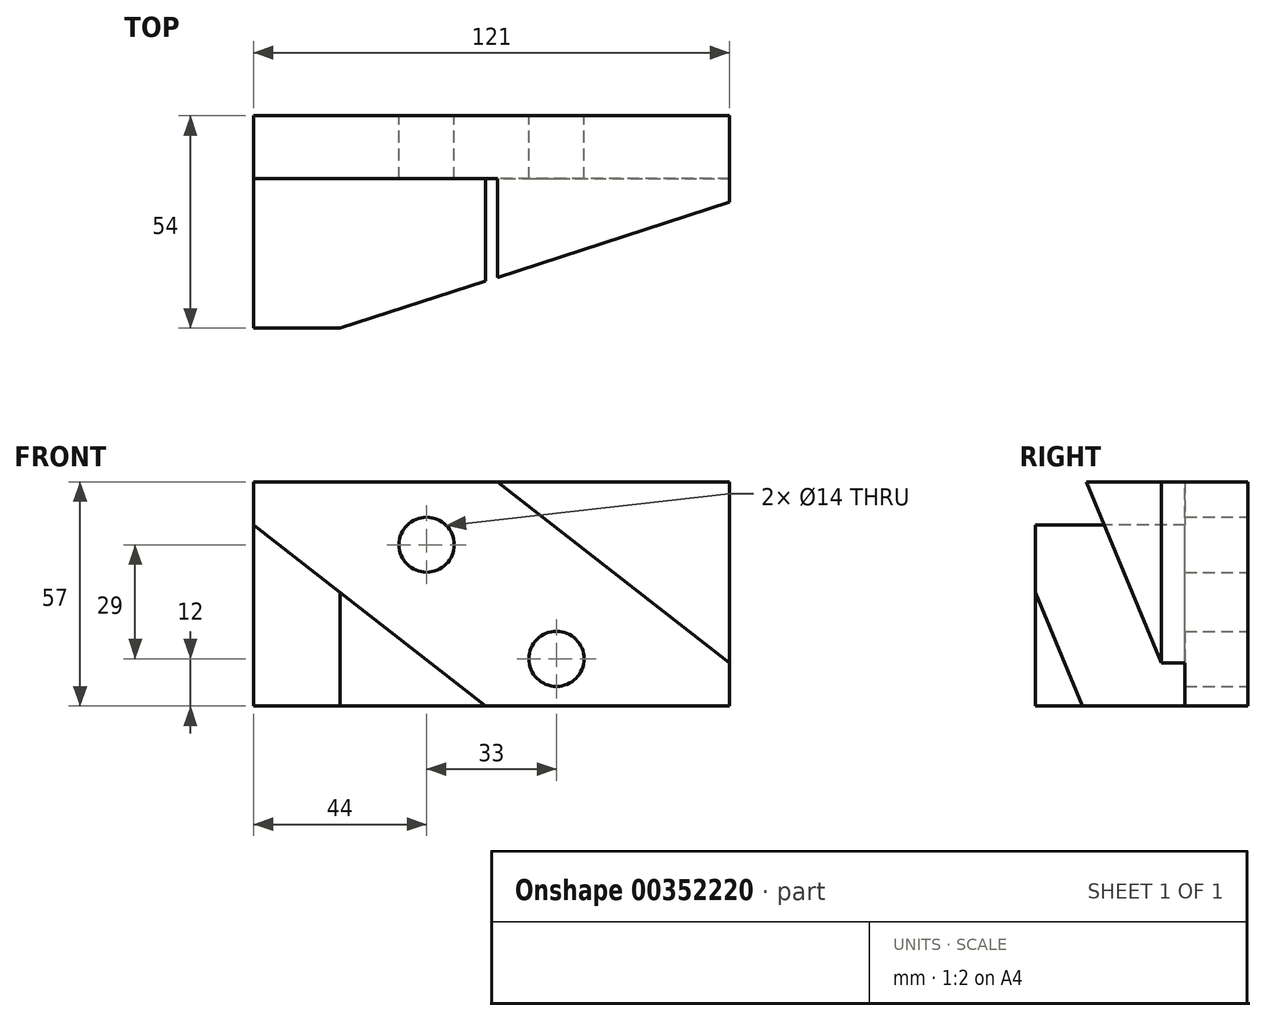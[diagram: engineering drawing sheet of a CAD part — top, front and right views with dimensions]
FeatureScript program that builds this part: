
annotation { "Feature Type Name" : "Feature", "Feature Type Description" : "" }
export const myFeature = defineFeature(function(context is Context, id is Id, definition is map)
    precondition{}
    {
        {
            var Q0;
            Q0=qCreatedBy(makeId("Front.planeOp"),FACE);
            var sketch = newSketch(context, id + "F0", { "sketchPlane" : qUnion([Q0])});
            skLineSegment(sketch, "E0", {"start": v(0, 0) * mm, "end": v(121, 0) * mm});
            skLineSegment(sketch, "E1", {"start": v(121, 0) * mm, "end": v(121, 57) * mm});
            skLineSegment(sketch, "E2", {"start": v(121, 57) * mm, "end": v(0, 57) * mm});
            skLineSegment(sketch, "E3", {"start": v(0, 57) * mm, "end": v(0, 0) * mm});
            skSolve(sketch);
        }
        {
            var Q0;
            Q0 = qSketchRegion(id + "F0", true);
            extrude(context, id + "F1", {"entities" : qUnion([Q0]), "depth" : 54 * mm});
        }
        {
            var Q0;
            Q0=makeQuery(id+"F1.opExtrude","SWEPT_FACE",FACE,{"disambiguationData":[OSD([sQuery(id+"F0.wireOp",EDGE,"E2")])]});
            var sketch = newSketch(context, id + "F2", { "sketchPlane" : qUnion([Q0])});
            skLineSegment(sketch, "E4", {"start": v(0, -54) * mm, "end": v(22, -54) * mm});
            skLineSegment(sketch, "E5", {"start": v(121, 0) * mm, "end": v(121, -16) * mm});
            skLineSegment(sketch, "E6", {"start": v(121, -16) * mm, "end": v(121, -22) * mm});
            skLineSegment(sketch, "E7", {"start": v(121, -22) * mm, "end": v(22, -54) * mm});
            skLineSegment(sketch, "E8", {"start": v(121, -22) * mm, "end": v(121, -54) * mm});
            skLineSegment(sketch, "E9", {"start": v(121, -54) * mm, "end": v(22, -54) * mm});
            skSolve(sketch);
        }
        {
            var Q0;
            Q0=makeQuery(id+"F2.imprint","IMPRINT",FACE,{"disambiguationData":[TD([[makeQuery(id+"F2.imprint","IMPRINT",EDGE,{"derivedFrom":sQuery(id+"F2.wireOp",EDGE,"E7")}),1.0]])]});
            extrude(context, id + "F3", {"entities" : qUnion([Q0]), "operationType" : NewBodyOperationType.REMOVE, "endBound" : BoundingType.THROUGH_ALL, "oppositeDirection" : true, "depth" : 25 * mm});
        }
        {
            var Q0;
            Q0=qCreatedBy(makeId("Front.planeOp"),FACE);
            var sketch = newSketch(context, id + "F4", { "sketchPlane" : qUnion([Q0])});
            skCircle(sketch, "E10", {"center": v(44, 41) * mm, "radius": 7 * mm});
            skCircle(sketch, "E11", {"center": v(77, 12) * mm, "radius": 7 * mm});
            skLineSegment(sketch, "E12.0.0", {"start": v(0, 0) * mm, "end": v(22, 0) * mm});
            skLineSegment(sketch, "E12.0.1", {"start": v(22, 0) * mm, "end": v(22, 57) * mm});
            skLineSegment(sketch, "E12.0.2", {"start": v(22, 57) * mm, "end": v(0, 57) * mm});
            skLineSegment(sketch, "E12.0.3", {"start": v(0, 57) * mm, "end": v(0, 0) * mm});
            skLineSegment(sketch, "E13.0", {"start": v(121, 57) * mm, "end": v(22, 57) * mm});
            skLineSegment(sketch, "E14.0.0", {"start": v(121, 0) * mm, "end": v(121, 57) * mm});
            skLineSegment(sketch, "E14.0.2", {"start": v(22, 57) * mm, "end": v(22, 0) * mm});
            skLineSegment(sketch, "E14.0.3", {"start": v(22, 0) * mm, "end": v(121, 0) * mm});
            skLineSegment(sketch, "E15", {"start": v(121, 57) * mm, "end": v(62, 57) * mm});
            skLineSegment(sketch, "E16", {"start": v(121, 57) * mm, "end": v(121, 11) * mm});
            skLineSegment(sketch, "E17", {"start": v(121, 11) * mm, "end": v(62, 57) * mm});
            skSolve(sketch);
        }
        {
            var Q0;
            Q0=makeQuery(id+"F4.imprint","IMPRINT",FACE,{"disambiguationData":[TD([[makeQuery(id+"F4.imprint","IMPRINT",EDGE,{"derivedFrom":sQuery(id+"F4.wireOp",EDGE,"E10")}),1.0]])]});
            var Q1;
            Q1=makeQuery(id+"F4.imprint","IMPRINT",FACE,{"disambiguationData":[TD([[makeQuery(id+"F4.imprint","IMPRINT",EDGE,{"derivedFrom":sQuery(id+"F4.wireOp",EDGE,"E11")}),1.0]])]});
            extrude(context, id + "F5", {"entities" : qUnion([Q0, Q1]), "operationType" : NewBodyOperationType.REMOVE, "endBound" : BoundingType.THROUGH_ALL, "depth" : 25 * mm});
        }
        {
            var Q0;
            Q0=makeQuery(id+"F1.opExtrude","CAP_FACE",FACE,{"disambiguationData":[OSD([sQuery(id+"F0.wireOp",EDGE,"E0"),sQuery(id+"F0.wireOp",EDGE,"E1"),sQuery(id+"F0.wireOp",EDGE,"E2"),sQuery(id+"F0.wireOp",EDGE,"E3")])],"isStart":false});
            var sketch = newSketch(context, id + "F6", { "sketchPlane" : qUnion([Q0])});
            skLineSegment(sketch, "E18.0.0", {"start": v(121, 0) * mm, "end": v(121, 11) * mm});
            skLineSegment(sketch, "E18.0.3", {"start": v(59, 0) * mm, "end": v(121, 0) * mm});
            skLineSegment(sketch, "E19", {"start": v(0, 0) * mm, "end": v(22, 0) * mm});
            skLineSegment(sketch, "E20", {"start": v(59, 0) * mm, "end": v(0, 46) * mm});
            skLineSegment(sketch, "E21", {"start": v(121, 11) * mm, "end": v(62, 57) * mm});
            skPoint(sketch, "E22.orphan", {"position": v(22, 0) * mm});
            skPoint(sketch, "E23.start.orphan", {"position": v(121, 57) * mm});
            skLineSegment(sketch, "E24", {"start": v(0, 46) * mm, "end": v(0, 57) * mm});
            skLineSegment(sketch, "E25", {"start": v(0, 57) * mm, "end": v(62, 57) * mm});
            skSolve(sketch);
        }
        {
            var Q0;
            Q0 = qSketchRegion(id + "F6", true);
            extrude(context, id + "F7", {"entities" : qUnion([Q0]), "operationType" : NewBodyOperationType.REMOVE, "oppositeDirection" : true, "depth" : 38 * mm});
        }
    });
